# Revit family: IS_ConnectAir_E0307_BIM_DE
name_source: partatom
category: Plumbing Fixtures
revit_build: Autodesk Revit MEP 2014 (Build: 20130308_1515(x64)
units: mm (PartAtom-declared; Revit-internal decimal feet)

## types (2) — shared parameters
Accessories = www.idealstandard.de\ersatzteile
AreaUnits = millimeters
Assembly Code = C1030200
AssetType = Fixed
Brand = Ideal Standard
CodePerformance = DIN EN 14688 CL 20, DIN EN 31
ConnectionType = Plumbing
Default Elevation = 850 mm
DrainSize = 42 mm
DurationUnit = year
E0309 = Yes
ExpectedLife = 25
Features = Connect Air 40cm handrinse washbasin, 1 taphole, with overflow
GrossWeight = 0
IfcExportAs = IfcSanitaryType
IfcExportType = WASHHANDBASIN
InstallationInstructions = www.idealstandard.de\produkte
LinearUnits = millimeters
ManufacturerURL = www.idealstandard.de
Material = Vitreous china
NBSDescription = Pedestal wash basins
NBSReference = 45-35-70/365
NettWeight = 7,7 kg
NominalHeight = 150 mm
NominalLength = 351 mm
NominalWidth = 401 mm
ProductInformation = www.idealstandard.de\produkte
Shape = Sculptured
Size = 400x350x150mm
Space = Internal
URL = www.idealstandard.com
Uniclass2015Code = Pr_40_20_96_63
Uniclass2015Title = Pedestal wash basins
Uniclass2015Version = Products v1.1
Version = 1
VolumeUnits = Litres
WarrantyDescription = Manufacturers Warranty
WarrantyDurationUnit = year
WashHandBasinMounting = i.e.Wall Hung
WashHandBasinType = Hand Rinse
zero-valued in all types: CWFU, Cost, HWFU, WFU

## per-type parameters (varying)
| type | BIMObjectName | BarCode | Color | Description | Finish | Model | ModelNumber | ModelReference | Name |
| E030701 - Connect Air 40cm handrinse washbasin, 1 taphole, with overflow | ISI_IdealStandard_PedestalWashBasins_ConnectAir_E030701 | 5017830514466 | white | E030701 Connect Air 40cm handrinse washbasin, 1 taphole, with overflow | white | E030701 | E030701 | E030701 Connect Air 40cm handrinse washbasin, 1 taphole, with overflow | PedestalWashBasins_ConnectAir_E030701_IdealStandard |
| E0307MA Connect Air 40cm handrinse washbasin, 1 taphole, with overflow | ISI_IdealStandard_PedestalWashBasins_ConnectAir_E0307MA | 5017830518433 | white with ideal plus | E0307MA Connect Air 40cm handrinse washbasin, 1 taphole, with overflow | white with ideal plus | E0307MA | E0307MA | E0307MA Connect Air 40cm handrinse washbasin, 1 taphole, with overflow | PedestalWashBasins_ConnectAir_E0307MA_IdealStandard |

## geometry (parser evidence)
native form markers: Sweep x4
no freeform markers — native parametric forms only
